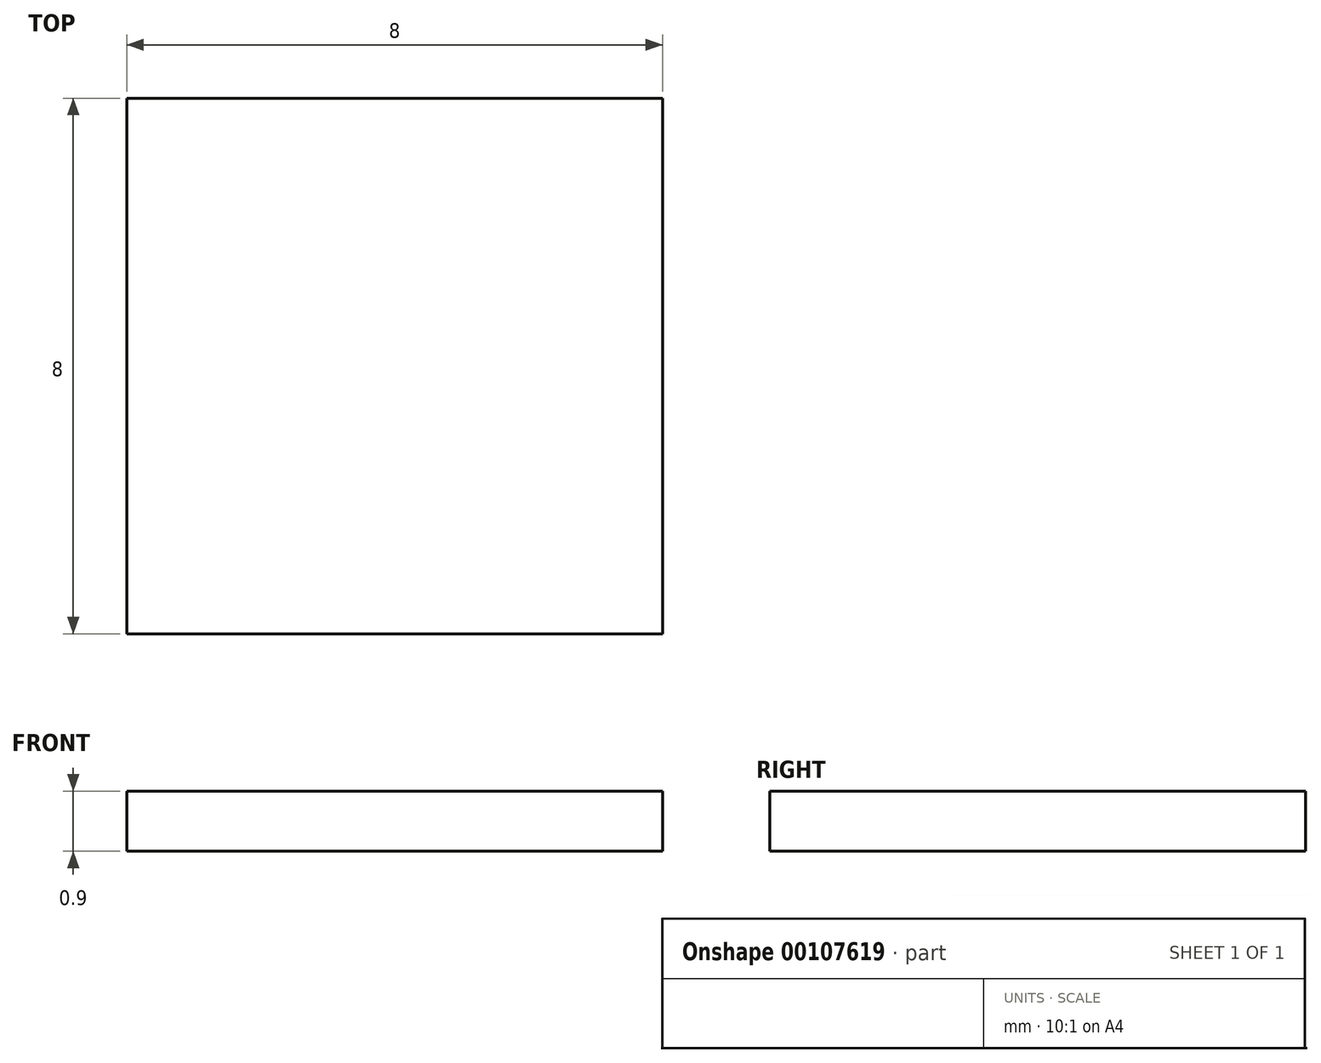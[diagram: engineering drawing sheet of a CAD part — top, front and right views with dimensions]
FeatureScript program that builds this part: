
annotation { "Feature Type Name" : "Feature", "Feature Type Description" : "" }
export const myFeature = defineFeature(function(context is Context, id is Id, definition is map)
    precondition{}
    {
        {
            var Q0;
            Q0=qCreatedBy(makeId("Top.planeOp"),FACE);
            var sketch = newSketch(context, id + "F0", { "sketchPlane" : qUnion([Q0])});
            skLineSegment(sketch, "E0.bottom", {"start": v(4, -4) * mm, "end": v(-4, -4) * mm});
            skLineSegment(sketch, "E0.top", {"start": v(4, 4) * mm, "end": v(-4, 4) * mm});
            skLineSegment(sketch, "E0.left", {"start": v(4, -4) * mm, "end": v(4, 4) * mm});
            skLineSegment(sketch, "E0.right", {"start": v(-4, -4) * mm, "end": v(-4, 4) * mm});
            skPoint(sketch, "E0.middle", {"position": v(0, 0) * mm});
            skCircle(sketch, "E1", {"center": v(0, 0) * mm, "radius": 1.9 * mm});
            skSolve(sketch);
        }
        {
            var Q0;
            Q0=makeQuery(id+"F0.imprint","IMPRINT",FACE,{"disambiguationData":[TD([[makeQuery(id+"F0.imprint","IMPRINT",EDGE,{"derivedFrom":sQuery(id+"F0.wireOp",EDGE,"E0.bottom")}),-1.0]])]});
            var Q1;
            Q1=makeQuery(id+"F0.imprint","IMPRINT",FACE,{"disambiguationData":[TD([[makeQuery(id+"F0.imprint","IMPRINT",EDGE,{"derivedFrom":sQuery(id+"F0.wireOp",EDGE,"E1")}),1.0]])]});
            extrude(context, id + "F1", {"entities" : qUnion([Q0, Q1]), "depth" : 0.9 * mm, "offsetDistance" : 25 * mm});
        }
    });
